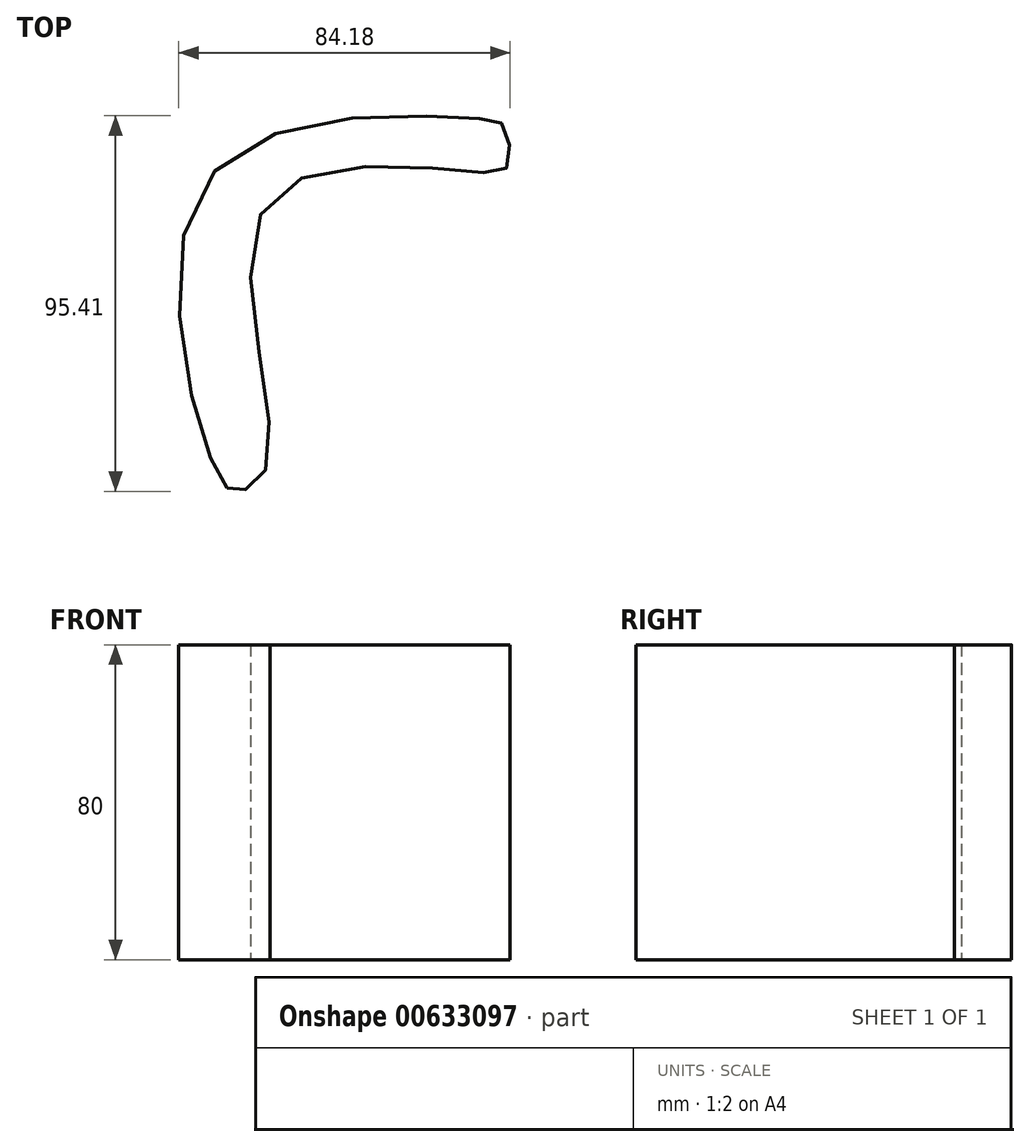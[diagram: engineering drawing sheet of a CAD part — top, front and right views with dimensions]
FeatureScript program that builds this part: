
annotation { "Feature Type Name" : "Feature", "Feature Type Description" : "" }
export const myFeature = defineFeature(function(context is Context, id is Id, definition is map)
    precondition{}
    {
        {
            var Q0;
            Q0=qCreatedBy(makeId("Top.planeOp"),FACE);
            var sketch = newSketch(context, id + "F0", { "sketchPlane" : qUnion([Q0])});
            skFitSpline(sketch, "E0", {"points": [v(47.48, 43.93) * mm, v(53.69, 41.86) * mm, v(54.87, 32.39) * mm, v(46.88, 30.32) * mm, v(-6.36, 22.63) * mm, v(-6.06, -42.45) * mm, v(-13.75, -50.73) * mm, v(-19.37, -45.7) * mm, v(-20.85, 29.43) * mm, v(47.48, 43.93) * mm]});
            skSolve(sketch);
        }
        {
            var Q0;
            Q0=makeQuery(id+"F0.imprint","IMPRINT",FACE,{"disambiguationData":[TD([[makeQuery(id+"F0.imprint","IMPRINT",EDGE,{"derivedFrom":sQuery(id+"F0.wireOp",EDGE,"E0")}),-1.0]])]});
            extrude(context, id + "F1", {"entities" : qUnion([Q0]), "depth" : 80 * mm, "offsetDistance" : 25 * mm});
        }
    });
